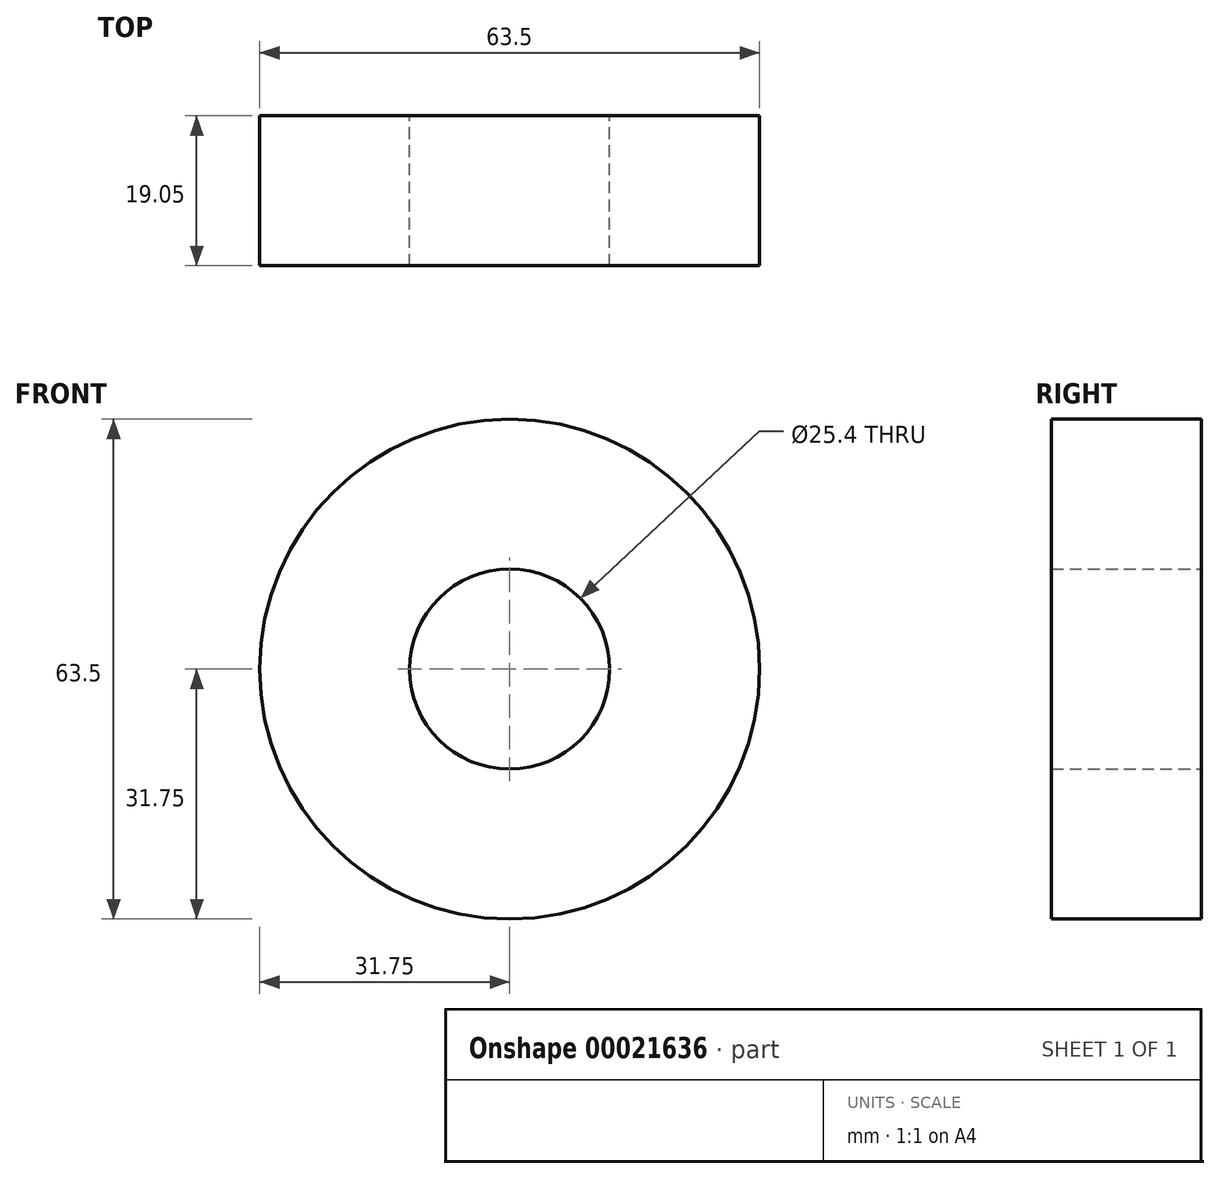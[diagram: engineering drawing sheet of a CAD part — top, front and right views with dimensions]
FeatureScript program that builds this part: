
annotation { "Feature Type Name" : "Feature", "Feature Type Description" : "" }
export const myFeature = defineFeature(function(context is Context, id is Id, definition is map)
    precondition{}
    {
        {
            var Q0;
            Q0=qCreatedBy(makeId("Front.planeOp"),FACE);
            var sketch = newSketch(context, id + "F0", { "sketchPlane" : qUnion([Q0])});
            skCircle(sketch, "E0", {"center": v(0, 0) * mm, "radius": 12.7 * mm});
            skCircle(sketch, "E1", {"center": v(0, 0) * mm, "radius": 31.75 * mm});
            skSolve(sketch);
        }
        {
            var Q0;
            Q0=makeQuery(id+"F0.imprint","IMPRINT",FACE,{"disambiguationData":[TD([[makeQuery(id+"F0.imprint","IMPRINT",EDGE,{"derivedFrom":sQuery(id+"F0.wireOp",EDGE,"E0")}),-1.0]])]});
            extrude(context, id + "F1", {"entities" : qUnion([Q0]), "depth" : 19.05 * mm});
        }
    });
